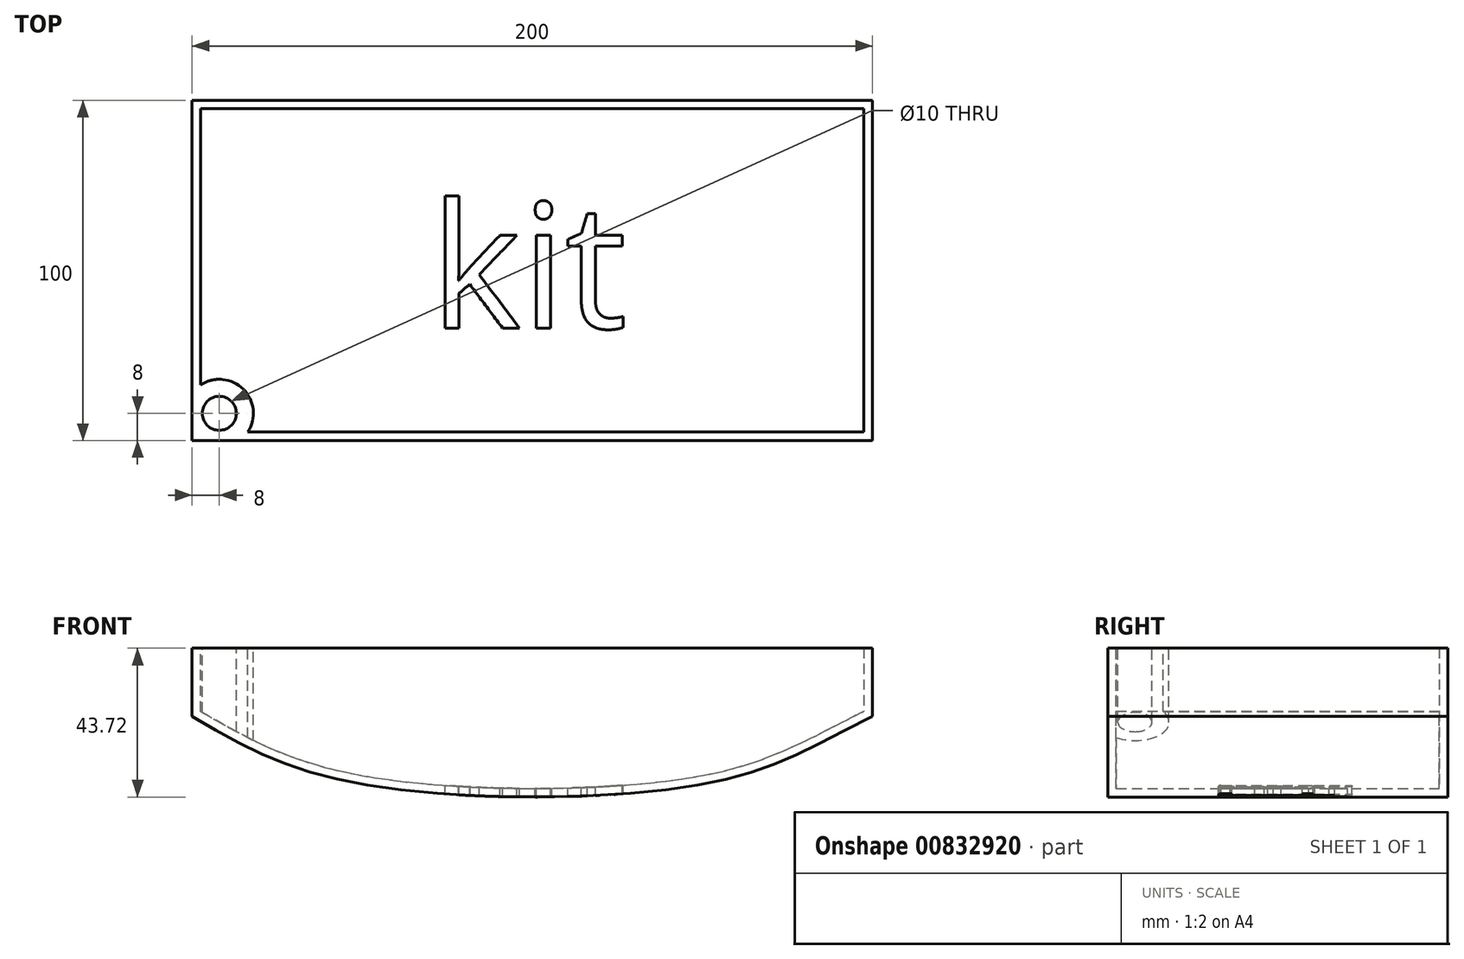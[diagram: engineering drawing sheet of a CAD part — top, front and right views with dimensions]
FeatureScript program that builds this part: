
annotation { "Feature Type Name" : "Feature", "Feature Type Description" : "" }
export const myFeature = defineFeature(function(context is Context, id is Id, definition is map)
    precondition{}
    {
        {
            var Q0;
            Q0=qCreatedBy(makeId("Front.planeOp"),FACE);
            var sketch = newSketch(context, id + "F0", { "sketchPlane" : qUnion([Q0])});
            skLineSegment(sketch, "E0.bottom", {"start": v(-100, 20) * mm, "end": v(100, 20) * mm});
            skLineSegment(sketch, "E0.left", {"start": v(-100, 20) * mm, "end": v(-100, 0) * mm});
            skLineSegment(sketch, "E0.right", {"start": v(100, 20) * mm, "end": v(100, 0) * mm});
            skFitSpline(sketch, "E1", {"points": [v(-100, 0) * mm, v(-50, -20) * mm, v(50, -20) * mm, v(100, 0) * mm], "startDerivative": vector(165.7, -98.56) * mm, "endDerivative": vector(203.67, 104.03) * mm});
            skPoint(sketch, "E2", {"position": v(0, 20) * mm});
            skPoint(sketch, "E3.orphan", {"position": v(-100, -20) * mm});
            skSolve(sketch);
        }
        {
            var Q0;
            Q0=makeQuery(id+"F0.imprint","IMPRINT",FACE,{"disambiguationData":[TD([[makeQuery(id+"F0.imprint","IMPRINT",EDGE,{"derivedFrom":sQuery(id+"F0.wireOp",EDGE,"E0.bottom")}),-1.0]])]});
            extrude(context, id + "F1", {"entities" : qUnion([Q0]), "depth" : 50 * mm, "offsetDistance" : 25 * mm, "hasSecondDirection" : true, "secondDirectionOppositeDirection" : true, "secondDirectionDepth" : 50 * mm});
        }
        {
            var Q0;
            Q0=makeQuery(id+"F1.opExtrude","SWEPT_FACE",FACE,{"disambiguationData":[OSD([sQuery(id+"F0.wireOp",EDGE,"E0.bottom")])]});
            shell(context, id + "F2", {"entities" : qUnion([Q0]), "thickness" : 2.5 * mm});
        }
        {
            var Q0;
            Q0=makeQuery(id+"F1.opExtrude","SWEPT_FACE",FACE,{"disambiguationData":[OSD([sQuery(id+"F0.wireOp",EDGE,"E0.bottom")])]});
            var sketch = newSketch(context, id + "F3", { "sketchPlane" : qUnion([Q0])});
            skCircle(sketch, "E4", {"center": v(-92, -42) * mm, "radius": 10 * mm});
            skCircle(sketch, "E5", {"center": v(-92, -42) * mm, "radius": 5 * mm});
            skSolve(sketch);
        }
        {
            var Q0;
            Q0 = qSketchRegion(id + "F3", true);
            extrude(context, id + "F4", {"entities" : qUnion([Q0]), "operationType" : NewBodyOperationType.ADD, "endBound" : BoundingType.UP_TO_NEXT, "oppositeDirection" : true, "depth" : 25 * mm, "offsetDistance" : 25 * mm});
        }
        {
            var Q0;
            Q0=qCreatedBy(makeId("Top.planeOp"),FACE);
            var sketch = newSketch(context, id + "F5", { "sketchPlane" : qUnion([Q0])});
            skText(sketch, "E6", { "text": "kit", "fontName": "OpenSans-Regular.ttf"});
            const initialGuessF5  = {"E6": [-0.03, -0.01697, 1, 0, 0.03678]};
            skSetInitialGuess(sketch, initialGuessF5);
            skSolve(sketch);
        }
        {
            var Q0;
            Q0 = qSketchRegion(id + "F5", true);
            var Q1;
            {var subQ2=sQuery(id+"F0.wireOp",EDGE,"E0.left");var subQ3=makeQuery(id+"F2.opShell","OFFSET_FACE",FACE,{"disambiguationData":[OSD([subQ2])]});var subQ4=sQuery(id+"F0.wireOp",EDGE,"E1");Q1=makeQuery(id+"F9rXrLz0a7ynBXh_1.1.FzhC19gK4xPjla6_1.1.F4.boolean.opBoolean","SPLIT",FACE,{"disambiguationData":[TD([subQ3])],"derivedFrom":makeQuery(id+"F9rXrLz0a7ynBXh_1.1.F4.boolean.opBoolean","SPLIT",FACE,{"disambiguationData":[TD([subQ3])],"derivedFrom":makeQuery(id+"FzhC19gK4xPjla6_1.1.F4.boolean.opBoolean","SPLIT",FACE,{"disambiguationData":[TD([subQ3])],"derivedFrom":makeQuery(id+"F4.boolean.opBoolean","SPLIT",FACE,{"disambiguationData":[TD([subQ3])],"derivedFrom":makeQuery(id+"F2.opShell","OFFSET_FACE",FACE,{"disambiguationData":[OSD([subQ4])]})})})})});}
            var Q2;
            Q2=makeQuery(id+"F1.opExtrude","SWEPT_BODY",BODY,{"disambiguationData":[OSD([sQuery(id+"F0.wireOp",EDGE,"E0.bottom"),sQuery(id+"F0.wireOp",EDGE,"E0.left"),sQuery(id+"F0.wireOp",EDGE,"E0.right"),sQuery(id+"F0.wireOp",EDGE,"E1")])]});
            extrude(context, id + "F6", {"entities" : qUnion([Q0]), "operationType" : NewBodyOperationType.REMOVE, "endBound" : BoundingType.THROUGH_ALL, "oppositeDirection" : true, "depth" : 25 * mm, "endBoundEntityFace" : qUnion([Q1]), "endBoundEntityBody" : qUnion([Q2]), "offsetDistance" : 25 * mm});
        }
    });
